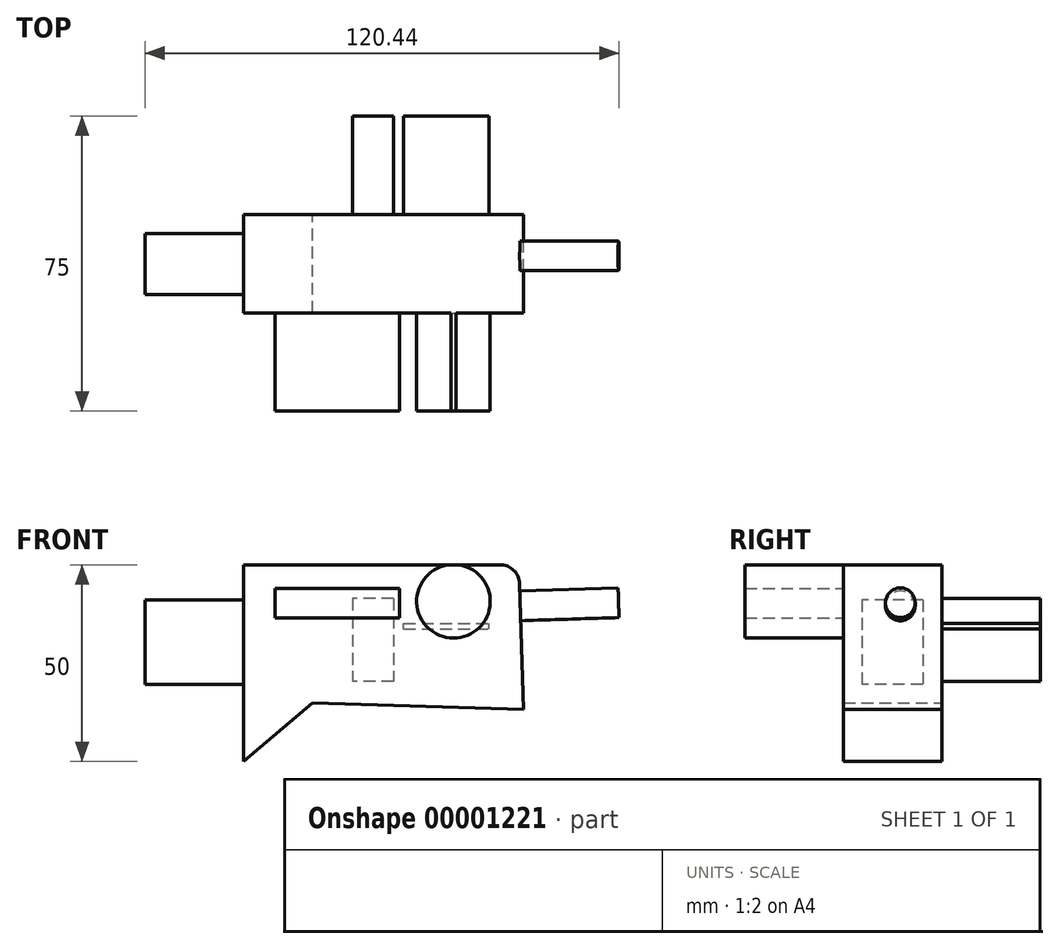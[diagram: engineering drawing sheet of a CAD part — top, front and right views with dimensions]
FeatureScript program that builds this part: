
annotation { "Feature Type Name" : "Feature", "Feature Type Description" : "" }
export const myFeature = defineFeature(function(context is Context, id is Id, definition is map)
    precondition{}
    {
        {
            var Q0;
            Q0=qCreatedBy(makeId("Front.planeOp"),FACE);
            var sketch = newSketch(context, id + "F0", { "sketchPlane" : qUnion([Q0])});
            skLineSegment(sketch, "E0", {"start": v(0, 0) * mm, "end": v(0, 50) * mm});
            skLineSegment(sketch, "E1", {"start": v(0, 50) * mm, "end": v(70, 50) * mm});
            skLineSegment(sketch, "E2", {"start": v(70, 50) * mm, "end": v(71.18, 13.23) * mm});
            skLineSegment(sketch, "E3", {"start": v(71.18, 13.23) * mm, "end": v(17.63, 14.95) * mm});
            skLineSegment(sketch, "E4", {"start": v(17.63, 14.95) * mm, "end": v(0, 0) * mm});
            skSolve(sketch);
        }
        {
            var Q0;
            Q0=makeQuery(id+"F0.imprint","IMPRINT",FACE,{"disambiguationData":[TD([[makeQuery(id+"F0.imprint","IMPRINT",EDGE,{"derivedFrom":sQuery(id+"F0.wireOp",EDGE,"E0")}),-1.0]])]});
            extrude(context, id + "F1", {"entities" : qUnion([Q0]), "depth" : 25 * mm, "offsetDistance" : 25 * mm});
        }
        {
            var Q0;
            Q0=makeQuery(id+"F1.opExtrude","SWEPT_EDGE",EDGE,{"disambiguationData":[OSD([sQuery(id+"F0.wireOp",EDGE,"E1"),sQuery(id+"F0.wireOp",EDGE,"E2")])]});
            fillet(context, id + "F2", {"entities" : qUnion([Q0]), "radius" : 5 * mm, "tangentPropagation" : true, "allowEdgeOverflow" : false});
        }
        {
            var Q0;
            Q0=makeQuery(id+"F1.opExtrude","CAP_FACE",FACE,{"disambiguationData":[OSD([sQuery(id+"F0.wireOp",EDGE,"E0"),sQuery(id+"F0.wireOp",EDGE,"E1"),sQuery(id+"F0.wireOp",EDGE,"E2"),sQuery(id+"F0.wireOp",EDGE,"E3"),sQuery(id+"F0.wireOp",EDGE,"E4")])],"isStart":false});
            var sketch = newSketch(context, id + "F3", { "sketchPlane" : qUnion([Q0])});
            skLineSegment(sketch, "E5.bottom", {"start": v(39.65, 36.44) * mm, "end": v(8.08, 36.44) * mm});
            skLineSegment(sketch, "E5.top", {"start": v(39.65, 43.98) * mm, "end": v(8.08, 43.98) * mm});
            skLineSegment(sketch, "E5.left", {"start": v(39.65, 36.44) * mm, "end": v(39.65, 43.98) * mm});
            skLineSegment(sketch, "E5.right", {"start": v(8.08, 36.44) * mm, "end": v(8.08, 43.98) * mm});
            skSolve(sketch);
        }
        {
            var Q0;
            Q0=makeQuery(id+"F3.imprint","IMPRINT",FACE,{"disambiguationData":[TD([[makeQuery(id+"F3.imprint","IMPRINT",EDGE,{"derivedFrom":sQuery(id+"F3.wireOp",EDGE,"E5.bottom")}),-1.0]])]});
            var Q1;
            Q1 = qSketchRegion(id + "F3", true);
            extrude(context, id + "F4", {"entities" : qUnion([Q0, Q1]), "operationType" : NewBodyOperationType.ADD, "depth" : 25 * mm, "offsetDistance" : 25 * mm});
        }
        {
            var Q0;
            Q0=makeQuery(id+"F1.opExtrude","CAP_FACE",FACE,{"disambiguationData":[OSD([sQuery(id+"F0.wireOp",EDGE,"E0"),sQuery(id+"F0.wireOp",EDGE,"E1"),sQuery(id+"F0.wireOp",EDGE,"E2"),sQuery(id+"F0.wireOp",EDGE,"E3"),sQuery(id+"F0.wireOp",EDGE,"E4")])],"isStart":true});
            var sketch = newSketch(context, id + "F5", { "sketchPlane" : qUnion([Q0])});
            skLineSegment(sketch, "E6.bottom", {"start": v(-40.75, 33.63) * mm, "end": v(-62.46, 33.63) * mm});
            skLineSegment(sketch, "E6.top", {"start": v(-40.75, 35.1) * mm, "end": v(-62.46, 35.1) * mm});
            skLineSegment(sketch, "E6.left", {"start": v(-40.75, 33.63) * mm, "end": v(-40.75, 35.1) * mm});
            skLineSegment(sketch, "E6.right", {"start": v(-62.46, 33.63) * mm, "end": v(-62.46, 35.1) * mm});
            skLineSegment(sketch, "E7.bottom", {"start": v(-38.14, 41.4) * mm, "end": v(-27.73, 41.4) * mm});
            skLineSegment(sketch, "E7.top", {"start": v(-38.14, 20.35) * mm, "end": v(-27.73, 20.35) * mm});
            skLineSegment(sketch, "E7.left", {"start": v(-38.14, 41.4) * mm, "end": v(-38.14, 20.35) * mm});
            skLineSegment(sketch, "E7.right", {"start": v(-27.73, 41.4) * mm, "end": v(-27.73, 20.35) * mm});
            skSolve(sketch);
        }
        {
            var Q0;
            Q0 = qSketchRegion(id + "F5", true);
            extrude(context, id + "F6", {"entities" : qUnion([Q0]), "operationType" : NewBodyOperationType.ADD, "depth" : 25 * mm, "offsetDistance" : 25 * mm});
        }
        {
            var Q0;
            Q0=makeQuery(id+"F1.opExtrude","CAP_FACE",FACE,{"disambiguationData":[OSD([sQuery(id+"F0.wireOp",EDGE,"E0"),sQuery(id+"F0.wireOp",EDGE,"E1"),sQuery(id+"F0.wireOp",EDGE,"E2"),sQuery(id+"F0.wireOp",EDGE,"E3"),sQuery(id+"F0.wireOp",EDGE,"E4")])],"isStart":false});
            var sketch = newSketch(context, id + "F7", { "sketchPlane" : qUnion([Q0])});
            skCircle(sketch, "E8", {"center": v(53.38, 40.68) * mm, "radius": 9.34 * mm});
            skSolve(sketch);
        }
        {
            var Q0;
            {var subQ0=sQuery(id+"F7.wireOp",EDGE,"E8");var subQ1=makeQuery(id+"F1.opExtrude","CAP_EDGE",EDGE,{"disambiguationData":[OSD([sQuery(id+"F0.wireOp",EDGE,"E1")])],"isStart":false});var subQ2=makeQuery(id+"F7.imprint","INTERSECT",VERTEX,{"disambiguationData":[OD(0.0)],"derivedFrom":[subQ1,subQ0]});Q0=makeQuery(id+"F7.imprint","IMPRINT",FACE,{"disambiguationData":[TD([[makeQuery(id+"F7.imprint","IMPRINT",EDGE,{"disambiguationData":[TD([[subQ2,-1.0]])],"derivedFrom":subQ0}),1.0]])]});}
            extrude(context, id + "F8", {"entities" : qUnion([Q0]), "operationType" : NewBodyOperationType.ADD, "depth" : 25 * mm, "offsetDistance" : 25 * mm});
        }
        {
            var Q0;
            Q0=makeQuery(id+"F1.opExtrude","SWEPT_FACE",FACE,{"disambiguationData":[OSD([sQuery(id+"F0.wireOp",EDGE,"E2")])]});
            var sketch = newSketch(context, id + "F9", { "sketchPlane" : qUnion([Q0])});
            skCircle(sketch, "E9", {"center": v(-10.54, 37.26) * mm, "radius": 3.77 * mm});
            skSolve(sketch);
        }
        {
            var Q0;
            Q0 = qSketchRegion(id + "F9", true);
            extrude(context, id + "F10", {"entities" : qUnion([Q0]), "operationType" : NewBodyOperationType.ADD, "depth" : 25 * mm, "offsetDistance" : 25 * mm});
        }
        {
            var Q0;
            Q0=makeQuery(id+"F1.opExtrude","SWEPT_FACE",FACE,{"disambiguationData":[OSD([sQuery(id+"F0.wireOp",EDGE,"E0")])]});
            var sketch = newSketch(context, id + "F11", { "sketchPlane" : qUnion([Q0])});
            skLineSegment(sketch, "E10.bottom", {"start": v(4.83, 41.06) * mm, "end": v(20.33, 41.06) * mm});
            skLineSegment(sketch, "E10.top", {"start": v(4.83, 19.53) * mm, "end": v(20.33, 19.53) * mm});
            skLineSegment(sketch, "E10.left", {"start": v(4.83, 41.06) * mm, "end": v(4.83, 19.53) * mm});
            skLineSegment(sketch, "E10.right", {"start": v(20.33, 41.06) * mm, "end": v(20.33, 19.53) * mm});
            skSolve(sketch);
        }
        {
            var Q0;
            Q0=makeQuery(id+"F11.imprint","IMPRINT",FACE,{"disambiguationData":[TD([[makeQuery(id+"F11.imprint","IMPRINT",EDGE,{"derivedFrom":sQuery(id+"F11.wireOp",EDGE,"E10.bottom")}),-1.0]])]});
            extrude(context, id + "F12", {"entities" : qUnion([Q0]), "operationType" : NewBodyOperationType.ADD, "depth" : 25 * mm, "offsetDistance" : 25 * mm});
        }
    });
